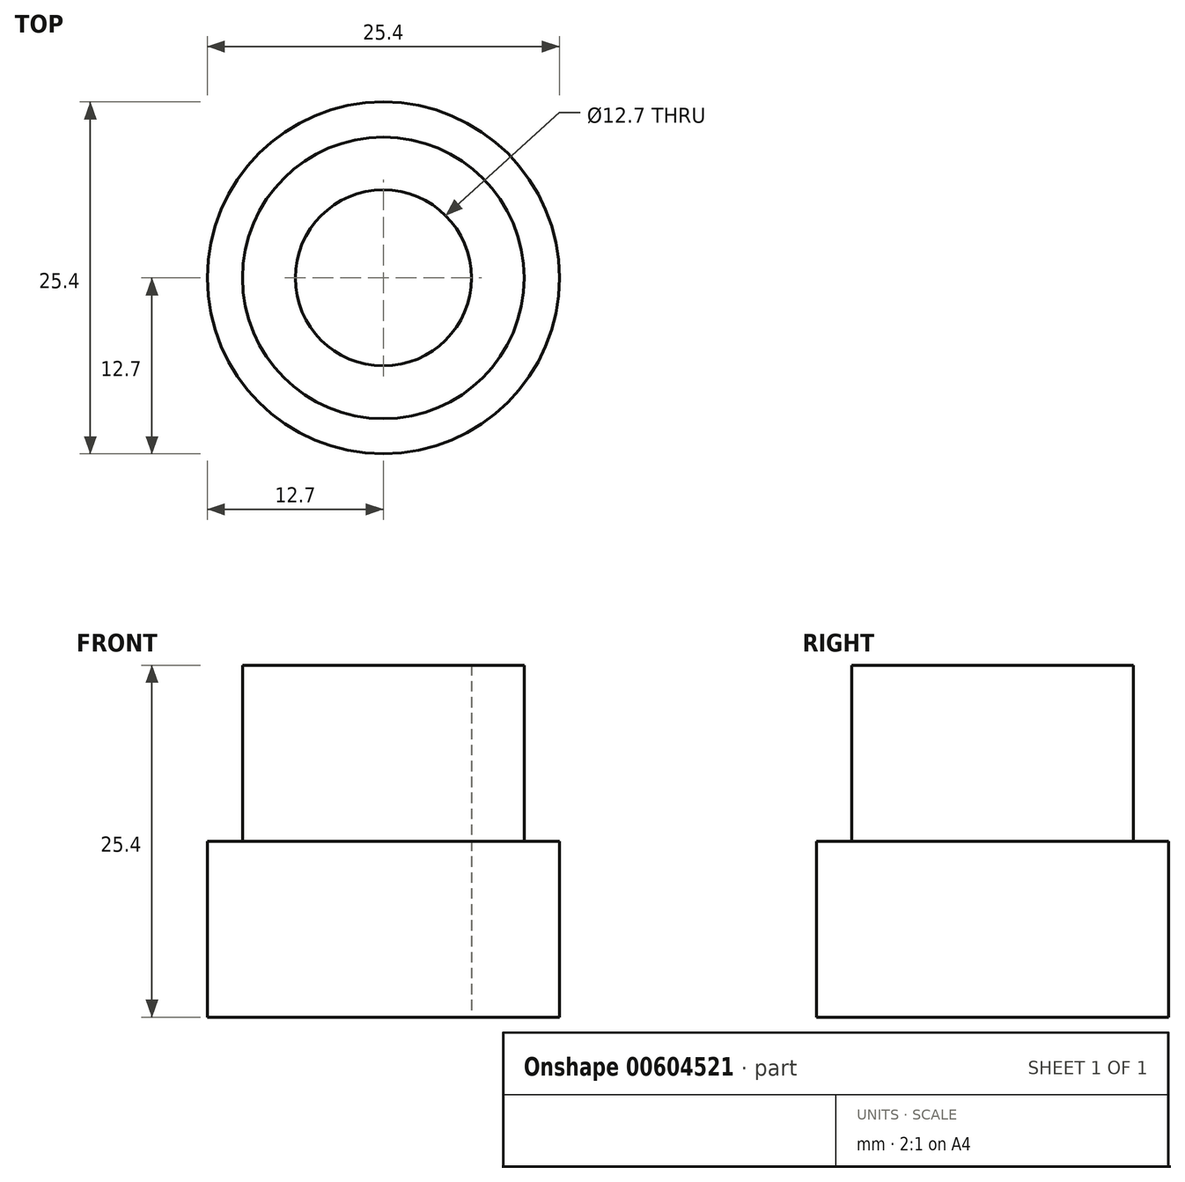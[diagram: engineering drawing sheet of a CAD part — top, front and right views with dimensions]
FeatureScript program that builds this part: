
annotation { "Feature Type Name" : "Feature", "Feature Type Description" : "" }
export const myFeature = defineFeature(function(context is Context, id is Id, definition is map)
    precondition{}
    {
        {
            var Q0;
            Q0=qCreatedBy(makeId("Top.planeOp"),FACE);
            var sketch = newSketch(context, id + "F0", { "sketchPlane" : qUnion([Q0])});
            skCircle(sketch, "E0", {"center": v(0, 0) * mm, "radius": 6.35 * mm});
            skCircle(sketch, "E1", {"center": v(0, 0) * mm, "radius": 12.7 * mm});
            skSolve(sketch);
        }
        {
            var Q0;
            Q0=makeQuery(id+"F0.imprint","IMPRINT",FACE,{"disambiguationData":[TD([[makeQuery(id+"F0.imprint","IMPRINT",EDGE,{"derivedFrom":sQuery(id+"F0.wireOp",EDGE,"E0")}),-1.0]])]});
            var Q1;
            Q1=sQuery(id+"F0.wireOp",EDGE,"E0");
            var Q2;
            Q2=sQuery(id+"F0.wireOp",EDGE,"E1");
            extrude(context, id + "F1", {"entities" : qUnion([Q0]), "surfaceEntities" : qUnion([Q1, Q2]), "depth" : 12.7 * mm, "offsetDistance" : 25.4 * mm});
        }
        {
            var Q0;
            Q0=makeQuery(id+"F1.opExtrude","CAP_FACE",FACE,{"disambiguationData":[OSD([sQuery(id+"F0.wireOp",EDGE,"E0"),sQuery(id+"F0.wireOp",EDGE,"E1")])],"isStart":false});
            var sketch = newSketch(context, id + "F2", { "sketchPlane" : qUnion([Q0])});
            skCircle(sketch, "E2", {"center": v(0, 0) * mm, "radius": 10.16 * mm});
            skSolve(sketch);
        }
        {
            var Q0;
            Q0=makeQuery(id+"F2.imprint","IMPRINT",FACE,{"disambiguationData":[TD([[makeQuery(id+"F2.imprint","IMPRINT",EDGE,{"derivedFrom":sQuery(id+"F2.wireOp",EDGE,"E2")}),1.0]])]});
            extrude(context, id + "F3", {"entities" : qUnion([Q0]), "operationType" : NewBodyOperationType.ADD, "depth" : 12.7 * mm, "offsetDistance" : 25.4 * mm});
        }
    });
